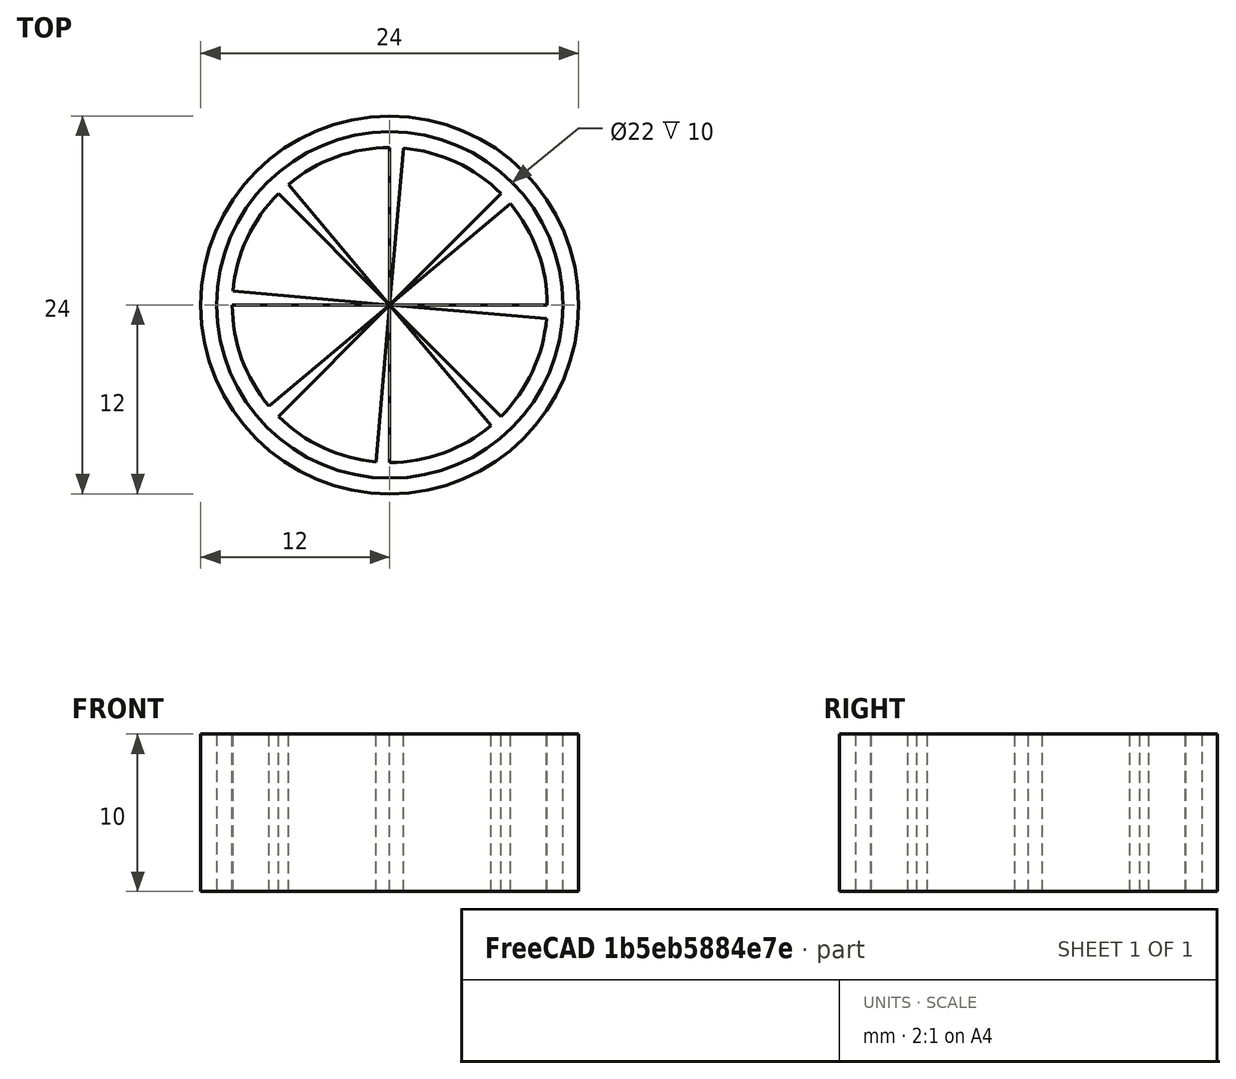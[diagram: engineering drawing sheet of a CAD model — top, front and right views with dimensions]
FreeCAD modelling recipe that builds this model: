
FCSTD DOCUMENT  (FreeCAD 0.21R33694 (Git))
Label: OJT1_T11R02_quesiitos
License: All rights reserved
LicenseURL: http://en.wikipedia.org/wiki/All_rights_reserved
objects: Part::Cylinder×10, Part::Cut×9
note: 19 computed .brp shape members not serialized (recipe doc carries the construction recipe); baked Part::Feature solids carry a one-line shape summary decoded from their .brp

FEATURE [Part::Cylinder] Cylinder
  Angle = 360
  AttacherType = Attacher::AttachEngine3D
  FirstAngle = 0
  Height = 10
  Radius = 12
  SecondAngle = 0
FEATURE [Part::Cylinder] Cylinder001
  Angle = 360
  AttacherType = Attacher::AttachEngine3D
  FirstAngle = 0
  Height = 10
  Radius = 11
  SecondAngle = 0
FEATURE [Part::Cylinder] Cylinder002
  Angle = 40
  AttacherType = Attacher::AttachEngine3D
  FirstAngle = 0
  Height = 10
  Radius = 10
  SecondAngle = 0
FEATURE [Part::Cylinder] Cylinder003
  Angle = 40
  AttacherType = Attacher::AttachEngine3D
  FirstAngle = 0
  Height = 10
  Placement = pos=(0,0,0) rot=(0,0,1;0.785398rad)
  Radius = 10
  SecondAngle = 0
FEATURE [Part::Cylinder] Cylinder004
  Angle = 40
  AttacherType = Attacher::AttachEngine3D
  FirstAngle = 0
  Height = 10
  Placement = pos=(0,0,0) rot=(0,0,1;1.5708rad)
  Radius = 10
  SecondAngle = 0
FEATURE [Part::Cylinder] Cylinder005
  Angle = 40
  AttacherType = Attacher::AttachEngine3D
  FirstAngle = 0
  Height = 10
  Placement = pos=(0,0,0) rot=(0,0,1;2.35619rad)
  Radius = 10
  SecondAngle = 0
FEATURE [Part::Cylinder] Cylinder006
  Angle = 40
  AttacherType = Attacher::AttachEngine3D
  FirstAngle = 0
  Height = 10
  Placement = pos=(0,0,0) rot=(0,0,1;3.14159rad)
  Radius = 10
  SecondAngle = 0
FEATURE [Part::Cylinder] Cylinder007
  Angle = 40
  AttacherType = Attacher::AttachEngine3D
  FirstAngle = 0
  Height = 10
  Placement = pos=(0,0,0) rot=(0,0,1;3.92699rad)
  Radius = 10
  SecondAngle = 0
FEATURE [Part::Cylinder] Cylinder008
  Angle = 40
  AttacherType = Attacher::AttachEngine3D
  FirstAngle = 0
  Height = 10
  Placement = pos=(0,0,0) rot=(0,0,1;4.71239rad)
  Radius = 10
  SecondAngle = 0
FEATURE [Part::Cylinder] Cylinder009
  Angle = 40
  AttacherType = Attacher::AttachEngine3D
  FirstAngle = 0
  Height = 10
  Placement = pos=(0,0,0) rot=(0,0,1;5.49779rad)
  Radius = 10
  SecondAngle = 0
FEATURE [Part::Cut] Cut
  Base = -> Cylinder001
  Refine = true
  Tool = -> Cylinder002
FEATURE [Part::Cut] Cut001
  Base = -> Cut
  Refine = true
  Tool = -> Cylinder009
FEATURE [Part::Cut] Cut002
  Base = -> Cut001
  Refine = true
  Tool = -> Cylinder008
FEATURE [Part::Cut] Cut003
  Base = -> Cut002
  Refine = true
  Tool = -> Cylinder007
FEATURE [Part::Cut] Cut004
  Base = -> Cut003
  Refine = true
  Tool = -> Cylinder006
FEATURE [Part::Cut] Cut005
  Base = -> Cut004
  Refine = true
  Tool = -> Cylinder005
FEATURE [Part::Cut] Cut006
  Base = -> Cut005
  Refine = true
  Tool = -> Cylinder004
FEATURE [Part::Cut] Cut007
  Base = -> Cut006
  Refine = true
  Tool = -> Cylinder003
FEATURE [Part::Cut] Cut008
  Base = -> Cylinder
  Refine = true
  Tool = -> Cut007
